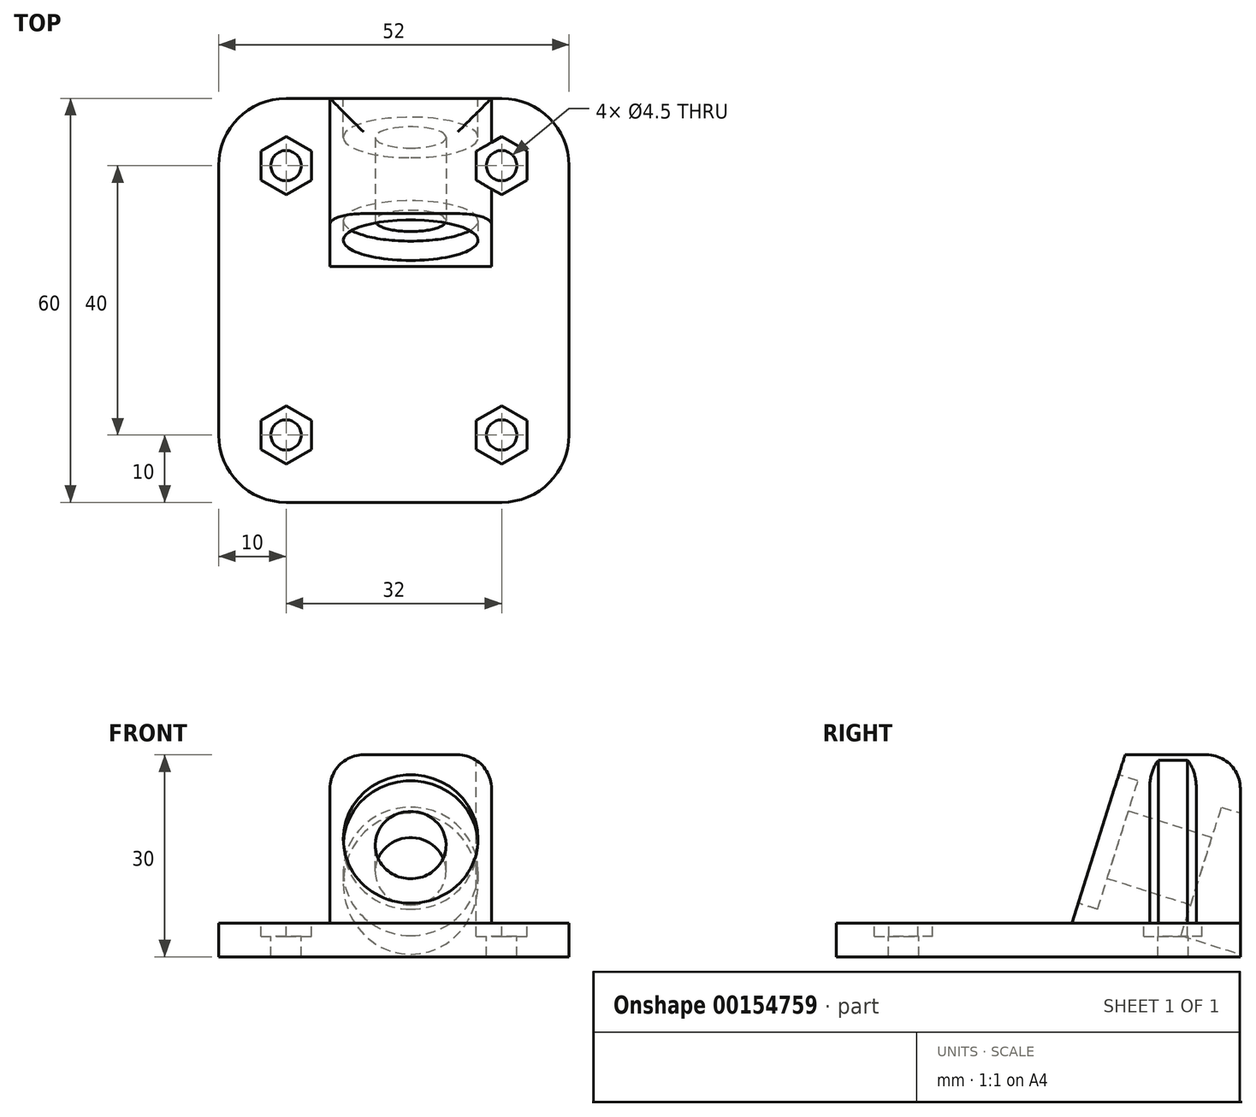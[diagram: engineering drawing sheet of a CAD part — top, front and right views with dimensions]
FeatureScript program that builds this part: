
annotation { "Feature Type Name" : "Feature", "Feature Type Description" : "" }
export const myFeature = defineFeature(function(context is Context, id is Id, definition is map)
    precondition{}
    {
        {
            var Q0;
            Q0=qCreatedBy(makeId("Top.planeOp"),FACE);
            var sketch = newSketch(context, id + "F0", { "sketchPlane" : qUnion([Q0])});
            skLineSegment(sketch, "E0.bottom", {"start": v(26, -30) * mm, "end": v(-26, -30) * mm});
            skLineSegment(sketch, "E0.top", {"start": v(26, 30) * mm, "end": v(-26, 30) * mm});
            skLineSegment(sketch, "E0.left", {"start": v(26, -30) * mm, "end": v(26, 30) * mm});
            skLineSegment(sketch, "E0.right", {"start": v(-26, -30) * mm, "end": v(-26, 30) * mm});
            skPoint(sketch, "E0.middle", {"position": v(0, 0) * mm});
            skSolve(sketch);
        }
        {
            var Q0;
            Q0=qSketchRegion(id+"F0",true);
            extrude(context, id + "F1", {"entities" : qUnion([Q0]), "depth" : 5 * mm});
        }
        {
            var Q0;
            Q0=makeQuery(id+"F1.opExtrude","SWEPT_EDGE",EDGE,{"disambiguationData":[OSD([sQuery(id+"F0.wireOp",EDGE,"E0.bottom"),sQuery(id+"F0.wireOp",EDGE,"E0.left")])]});
            var Q1;
            Q1=makeQuery(id+"F1.opExtrude","SWEPT_EDGE",EDGE,{"disambiguationData":[OSD([sQuery(id+"F0.wireOp",EDGE,"E0.bottom"),sQuery(id+"F0.wireOp",EDGE,"E0.right")])]});
            var Q2;
            Q2=makeQuery(id+"F1.opExtrude","SWEPT_EDGE",EDGE,{"disambiguationData":[OSD([sQuery(id+"F0.wireOp",EDGE,"E0.top"),sQuery(id+"F0.wireOp",EDGE,"E0.left")])]});
            var Q3;
            Q3=makeQuery(id+"F1.opExtrude","SWEPT_EDGE",EDGE,{"disambiguationData":[OSD([sQuery(id+"F0.wireOp",EDGE,"E0.top"),sQuery(id+"F0.wireOp",EDGE,"E0.right")])]});
            fillet(context, id + "F2", {"entities" : qUnion([Q0, Q1, Q2, Q3]), "radius" : 10 * mm, "tangentPropagation" : true, "allowEdgeOverflow" : false});
        }
        {
            var Q0;
            Q0=makeQuery(id+"F1.opExtrude","CAP_FACE",FACE,{"disambiguationData":[OSD([sQuery(id+"F0.wireOp",EDGE,"E0.bottom"),sQuery(id+"F0.wireOp",EDGE,"E0.top"),sQuery(id+"F0.wireOp",EDGE,"E0.left"),sQuery(id+"F0.wireOp",EDGE,"E0.right")])],"isStart":false});
            var sketch = newSketch(context, id + "F3", { "sketchPlane" : qUnion([Q0])});
            skCircle(sketch, "E1", {"center": v(16, -20) * mm, "radius": 2.25 * mm});
            skCircle(sketch, "E2.0.1.0", {"center": v(16, 20) * mm, "radius": 2.25 * mm});
            skCircle(sketch, "E2.1.0.0", {"center": v(-16, -20) * mm, "radius": 2.25 * mm});
            skCircle(sketch, "E2.1.1.0", {"center": v(-16, 20) * mm, "radius": 2.25 * mm});
            skLineSegment(sketch, "E2.direction1", {"start": v(16, -20) * mm, "end": v(-16, -20) * mm, "construction": true});
            skLineSegment(sketch, "E2.direction2", {"start": v(16, -20) * mm, "end": v(16, 20) * mm, "construction": true});
            skSolve(sketch);
        }
        {
            var Q0;
            Q0=makeQuery(id+"F3.imprint","IMPRINT",FACE,{"disambiguationData":[TD([[makeQuery(id+"F3.imprint","IMPRINT",EDGE,{"derivedFrom":sQuery(id+"F3.wireOp",EDGE,"E2.1.0.0")}),1.0]])]});
            var Q1;
            Q1=makeQuery(id+"F3.imprint","IMPRINT",FACE,{"disambiguationData":[TD([[makeQuery(id+"F3.imprint","IMPRINT",EDGE,{"derivedFrom":sQuery(id+"F3.wireOp",EDGE,"E1")}),1.0]])]});
            var Q2;
            Q2=makeQuery(id+"F3.imprint","IMPRINT",FACE,{"disambiguationData":[TD([[makeQuery(id+"F3.imprint","IMPRINT",EDGE,{"derivedFrom":sQuery(id+"F3.wireOp",EDGE,"E2.1.1.0")}),1.0]])]});
            var Q3;
            Q3=makeQuery(id+"F3.imprint","IMPRINT",FACE,{"disambiguationData":[TD([[makeQuery(id+"F3.imprint","IMPRINT",EDGE,{"derivedFrom":sQuery(id+"F3.wireOp",EDGE,"E2.0.1.0")}),1.0]])]});
            extrude(context, id + "F4", {"entities" : qUnion([Q0, Q1, Q2, Q3]), "operationType" : NewBodyOperationType.REMOVE, "oppositeDirection" : true, "depth" : 25 * mm});
        }
        {
            var Q0;
            Q0=makeQuery(id+"F1.opExtrude","CAP_FACE",FACE,{"disambiguationData":[OSD([sQuery(id+"F0.wireOp",EDGE,"E0.bottom"),sQuery(id+"F0.wireOp",EDGE,"E0.top"),sQuery(id+"F0.wireOp",EDGE,"E0.left"),sQuery(id+"F0.wireOp",EDGE,"E0.right")])],"isStart":false});
            var sketch = newSketch(context, id + "F5", { "sketchPlane" : qUnion([Q0])});
            skCircle(sketch, "E3.cCircle", {"center": v(-16, -20) * mm, "radius": 3.75 * mm, "construction": true});
            skLineSegment(sketch, "E3.0", {"start": v(-19.75, -17.83) * mm, "end": v(-16, -15.67) * mm});
            skLineSegment(sketch, "E3.1", {"start": v(-16, -15.67) * mm, "end": v(-12.25, -17.83) * mm});
            skLineSegment(sketch, "E3.2", {"start": v(-12.25, -17.83) * mm, "end": v(-12.25, -22.17) * mm});
            skLineSegment(sketch, "E3.3", {"start": v(-12.25, -22.17) * mm, "end": v(-16, -24.33) * mm});
            skLineSegment(sketch, "E3.4", {"start": v(-16, -24.33) * mm, "end": v(-19.75, -22.17) * mm});
            skLineSegment(sketch, "E3.5", {"start": v(-19.75, -22.17) * mm, "end": v(-19.75, -17.83) * mm});
            skPoint(sketch, "E3.0.midPoint", {"position": v(-17.88, -16.75) * mm});
            skLineSegment(sketch, "E4.0.1.0", {"start": v(-16, 24.33) * mm, "end": v(-12.25, 22.17) * mm});
            skLineSegment(sketch, "E4.0.1.1", {"start": v(-12.25, 22.17) * mm, "end": v(-12.25, 17.83) * mm});
            skLineSegment(sketch, "E4.0.1.2", {"start": v(-12.25, 17.83) * mm, "end": v(-16, 15.67) * mm});
            skLineSegment(sketch, "E4.0.1.3", {"start": v(-16, 15.67) * mm, "end": v(-19.75, 17.83) * mm});
            skLineSegment(sketch, "E4.0.1.4", {"start": v(-19.75, 17.83) * mm, "end": v(-19.75, 22.17) * mm});
            skLineSegment(sketch, "E4.0.1.5", {"start": v(-19.75, 22.17) * mm, "end": v(-16, 24.33) * mm});
            skLineSegment(sketch, "E4.1.0.0", {"start": v(16, -15.67) * mm, "end": v(19.75, -17.83) * mm});
            skLineSegment(sketch, "E4.1.0.1", {"start": v(19.75, -17.83) * mm, "end": v(19.75, -22.17) * mm});
            skLineSegment(sketch, "E4.1.0.2", {"start": v(19.75, -22.17) * mm, "end": v(16, -24.33) * mm});
            skLineSegment(sketch, "E4.1.0.3", {"start": v(16, -24.33) * mm, "end": v(12.25, -22.17) * mm});
            skLineSegment(sketch, "E4.1.0.4", {"start": v(12.25, -22.17) * mm, "end": v(12.25, -17.83) * mm});
            skLineSegment(sketch, "E4.1.0.5", {"start": v(12.25, -17.83) * mm, "end": v(16, -15.67) * mm});
            skLineSegment(sketch, "E4.1.1.0", {"start": v(16, 24.33) * mm, "end": v(19.75, 22.17) * mm});
            skLineSegment(sketch, "E4.1.1.1", {"start": v(19.75, 22.17) * mm, "end": v(19.75, 17.83) * mm});
            skLineSegment(sketch, "E4.1.1.2", {"start": v(19.75, 17.83) * mm, "end": v(16, 15.67) * mm});
            skLineSegment(sketch, "E4.1.1.3", {"start": v(16, 15.67) * mm, "end": v(12.25, 17.83) * mm});
            skLineSegment(sketch, "E4.1.1.4", {"start": v(12.25, 17.83) * mm, "end": v(12.25, 22.17) * mm});
            skLineSegment(sketch, "E4.1.1.5", {"start": v(12.25, 22.17) * mm, "end": v(16, 24.33) * mm});
            skLineSegment(sketch, "E4.direction1", {"start": v(-16, -15.96) * mm, "end": v(16, -15.96) * mm, "construction": true});
            skLineSegment(sketch, "E4.direction2", {"start": v(-16, -15.96) * mm, "end": v(-16, 24.04) * mm, "construction": true});
            skSolve(sketch);
        }
        {
            var Q0;
            Q0=qSketchRegion(id+"F5",true);
            extrude(context, id + "F6", {"entities" : qUnion([Q0]), "operationType" : NewBodyOperationType.REMOVE, "oppositeDirection" : true, "depth" : 2 * mm});
        }
        {
            var Q0;
            Q0=makeQuery(id+"F1.opExtrude","CAP_FACE",FACE,{"disambiguationData":[OSD([sQuery(id+"F0.wireOp",EDGE,"E0.bottom"),sQuery(id+"F0.wireOp",EDGE,"E0.top"),sQuery(id+"F0.wireOp",EDGE,"E0.left"),sQuery(id+"F0.wireOp",EDGE,"E0.right")])],"isStart":false});
            var sketch = newSketch(context, id + "F7", { "sketchPlane" : qUnion([Q0])});
            skLineSegment(sketch, "E5.bottom", {"start": v(14.5, 30) * mm, "end": v(-9.5, 30) * mm});
            skLineSegment(sketch, "E5.top", {"start": v(14.5, 5) * mm, "end": v(-9.5, 5) * mm});
            skLineSegment(sketch, "E5.left", {"start": v(14.5, 30) * mm, "end": v(14.5, 5) * mm});
            skLineSegment(sketch, "E5.right", {"start": v(-9.5, 30) * mm, "end": v(-9.5, 5) * mm});
            skPoint(sketch, "E5.middle", {"position": v(2.5, 17.5) * mm});
            skSolve(sketch);
        }
        {
            var Q0;
            Q0=qSketchRegion(id+"F7",true);
            extrude(context, id + "F8", {"entities" : qUnion([Q0]), "operationType" : NewBodyOperationType.ADD, "depth" : 25 * mm});
        }
        {
            var Q0;
            Q0=makeQuery(id+"F8.opExtrude","SWEPT_FACE",FACE,{"disambiguationData":[OSD([sQuery(id+"F7.wireOp",EDGE,"E5.right")])]});
            var sketch = newSketch(context, id + "F9", { "sketchPlane" : qUnion([Q0])});
            skLineSegment(sketch, "E6", {"start": v(-5, 5) * mm, "end": v(-12.88, 30) * mm});
            skLineSegment(sketch, "E7", {"start": v(-12.88, 30) * mm, "end": v(-5, 30) * mm});
            skLineSegment(sketch, "E8", {"start": v(-5, 30) * mm, "end": v(-5, 5) * mm});
            skSolve(sketch);
        }
        {
            var Q0;
            Q0=makeQuery(id+"F9.imprint","IMPRINT",FACE,{"disambiguationData":[TD([[makeQuery(id+"F9.imprint","IMPRINT",EDGE,{"derivedFrom":sQuery(id+"F9.wireOp",EDGE,"E6")}),-1.0]])]});
            extrude(context, id + "F10", {"entities" : qUnion([Q0]), "operationType" : NewBodyOperationType.REMOVE, "endBound" : BoundingType.THROUGH_ALL, "oppositeDirection" : true, "depth" : 25 * mm});
        }
        {
            var Q0;
            Q0=makeQuery(id+"F10.boolean.opBoolean","COPY",FACE,{"derivedFrom":makeQuery(id+"F10.opExtrude","SWEPT_FACE",FACE,{"disambiguationData":[OSD([sQuery(id+"F9.wireOp",EDGE,"E6")])]})});
            var sketch = newSketch(context, id + "F11", { "sketchPlane" : qUnion([Q0])});
            skLineSegment(sketch, "E9", {"start": v(-9.5, 6.27) * mm, "end": v(-9.5, 32.49) * mm});
            skLineSegment(sketch, "E10", {"start": v(-9.5, 32.49) * mm, "end": v(14.5, 32.49) * mm});
            skLineSegment(sketch, "E11", {"start": v(14.5, 32.49) * mm, "end": v(14.5, 6.27) * mm});
            skLineSegment(sketch, "E12", {"start": v(14.5, 6.27) * mm, "end": v(-9.5, 6.27) * mm});
            skCircle(sketch, "E13", {"center": v(2.5, 19.38) * mm, "radius": 5.25 * mm});
            skPoint(sketch, "E13.centerSnap0", {"position": v(2.5, 32.49) * mm});
            skPoint(sketch, "E13.centerSnap1", {"position": v(-9.5, 19.38) * mm});
            skSolve(sketch);
        }
        {
            var Q0;
            Q0=makeQuery(id+"F11.imprint","IMPRINT",FACE,{"disambiguationData":[TD([[makeQuery(id+"F11.imprint","IMPRINT",EDGE,{"derivedFrom":sQuery(id+"F11.wireOp",EDGE,"E13")}),1.0]])]});
            extrude(context, id + "F12", {"entities" : qUnion([Q0]), "operationType" : NewBodyOperationType.REMOVE, "endBound" : BoundingType.THROUGH_ALL, "oppositeDirection" : true, "depth" : 25 * mm});
        }
        {
            var Q0;
            Q0=makeQuery(id+"F10.boolean.opBoolean","COPY",FACE,{"derivedFrom":makeQuery(id+"F10.opExtrude","SWEPT_FACE",FACE,{"disambiguationData":[OSD([sQuery(id+"F9.wireOp",EDGE,"E6")])]})});
            var sketch = newSketch(context, id + "F13", { "sketchPlane" : qUnion([Q0])});
            skCircle(sketch, "E14", {"center": v(2.5, 19.38) * mm, "radius": 10 * mm});
            skSolve(sketch);
        }
        {
            var Q0;
            Q0=makeQuery(id+"F13.imprint","IMPRINT",FACE,{"disambiguationData":[TD([[makeQuery(id+"F13.imprint","IMPRINT",EDGE,{"derivedFrom":sQuery(id+"F13.wireOp",EDGE,"E14")}),1.0]])]});
            extrude(context, id + "F14", {"entities" : qUnion([Q0]), "operationType" : NewBodyOperationType.REMOVE, "oppositeDirection" : true, "depth" : 3 * mm});
        }
        {
            var Q0;
            Q0=makeQuery(id+"F10.boolean.opBoolean","COPY",FACE,{"derivedFrom":makeQuery(id+"F10.opExtrude","SWEPT_FACE",FACE,{"disambiguationData":[OSD([sQuery(id+"F9.wireOp",EDGE,"E6")])]})});
            cPlane(context, id + "F15", {"entities" : qUnion([Q0]), "cplaneType" : CPlaneType.OFFSET, "offset" : 28 * mm, "oppositeDirection" : true, "width" : 150 * mm, "height" : 150 * mm});
        }
        {
            var Q0;
            Q0=qCreatedBy(id+"F15.planeOp",FACE);
            var sketch = newSketch(context, id + "F16", { "sketchPlane" : qUnion([Q0])});
            skCircle(sketch, "E15", {"center": v(2.5, 19.38) * mm, "radius": 10 * mm});
            skSolve(sketch);
        }
        {
            var Q0;
            Q0=qSketchRegion(id+"F16",true);
            extrude(context, id + "F17", {"entities" : qUnion([Q0]), "operationType" : NewBodyOperationType.REMOVE, "depth" : 12 * mm});
        }
        {
            var Q0;
            Q0=qSketchRegion(id+"F5",true);
            extrude(context, id + "F18", {"entities" : qUnion([Q0]), "operationType" : NewBodyOperationType.REMOVE, "endBound" : BoundingType.THROUGH_ALL, "depth" : 25 * mm});
        }
        {
            var Q0;
            {var subQ0=sQuery(id+"F7.wireOp",EDGE,"E5.right");Q0=makeQuery(id+"F18.boolean.opBoolean","SPLIT",EDGE,{"disambiguationData":[TD([makeQuery(id+"F1.opExtrude","SWEPT_FACE",FACE,{"disambiguationData":[OSD([sQuery(id+"F0.wireOp",EDGE,"E0.top")])]})])],"derivedFrom":makeQuery(id+"F8.opExtrude","CAP_EDGE",EDGE,{"disambiguationData":[OSD([subQ0])],"isStart":false})});}
            var Q1;
            {var subQ0=sQuery(id+"F7.wireOp",EDGE,"E5.right");var subQ1=sQuery(id+"F5.wireOp",EDGE,"E4.0.1.2");Q1=makeQuery(id+"F18.boolean.opBoolean","SPLIT",EDGE,{"disambiguationData":[TD([makeQuery(id+"F6.boolean.opBoolean","COPY",FACE,{"derivedFrom":makeQuery(id+"F6.opExtrude","SWEPT_FACE",FACE,{"disambiguationData":[OSD([subQ1])]})})])],"derivedFrom":makeQuery(id+"F8.opExtrude","CAP_EDGE",EDGE,{"disambiguationData":[OSD([subQ0])],"isStart":false})});}
            var Q2;
            Q2=makeQuery(id+"F8.opExtrude","CAP_EDGE",EDGE,{"disambiguationData":[OSD([sQuery(id+"F7.wireOp",EDGE,"E5.left")])],"isStart":false});
            var Q3;
            Q3=makeQuery(id+"F8.opExtrude","CAP_EDGE",EDGE,{"disambiguationData":[OSD([sQuery(id+"F7.wireOp",EDGE,"E5.bottom")])],"isStart":false});
            var Q4;
            Q4=makeQuery(id+"F10.boolean.opBoolean","MERGE",EDGE,{"derivedFrom":[makeQuery(id+"F8.opExtrude","CAP_EDGE",EDGE,{"disambiguationData":[OSD([sQuery(id+"F7.wireOp",EDGE,"E5.top")])],"isStart":true}),makeQuery(id+"F10.opExtrude","SWEPT_EDGE",EDGE,{"disambiguationData":[OSD([sQuery(id+"F7.wireOp",EDGE,"E5.right"),sQuery(id+"F9.wireOp",EDGE,"E6"),sQuery(id+"F9.wireOp",EDGE,"E8")])]})]});
            fillet(context, id + "F19", {"entities" : qUnion([Q0, Q1, Q2, Q3, Q4]), "radius" : 5 * mm, "tangentPropagation" : true, "allowEdgeOverflow" : false});
        }
    });
